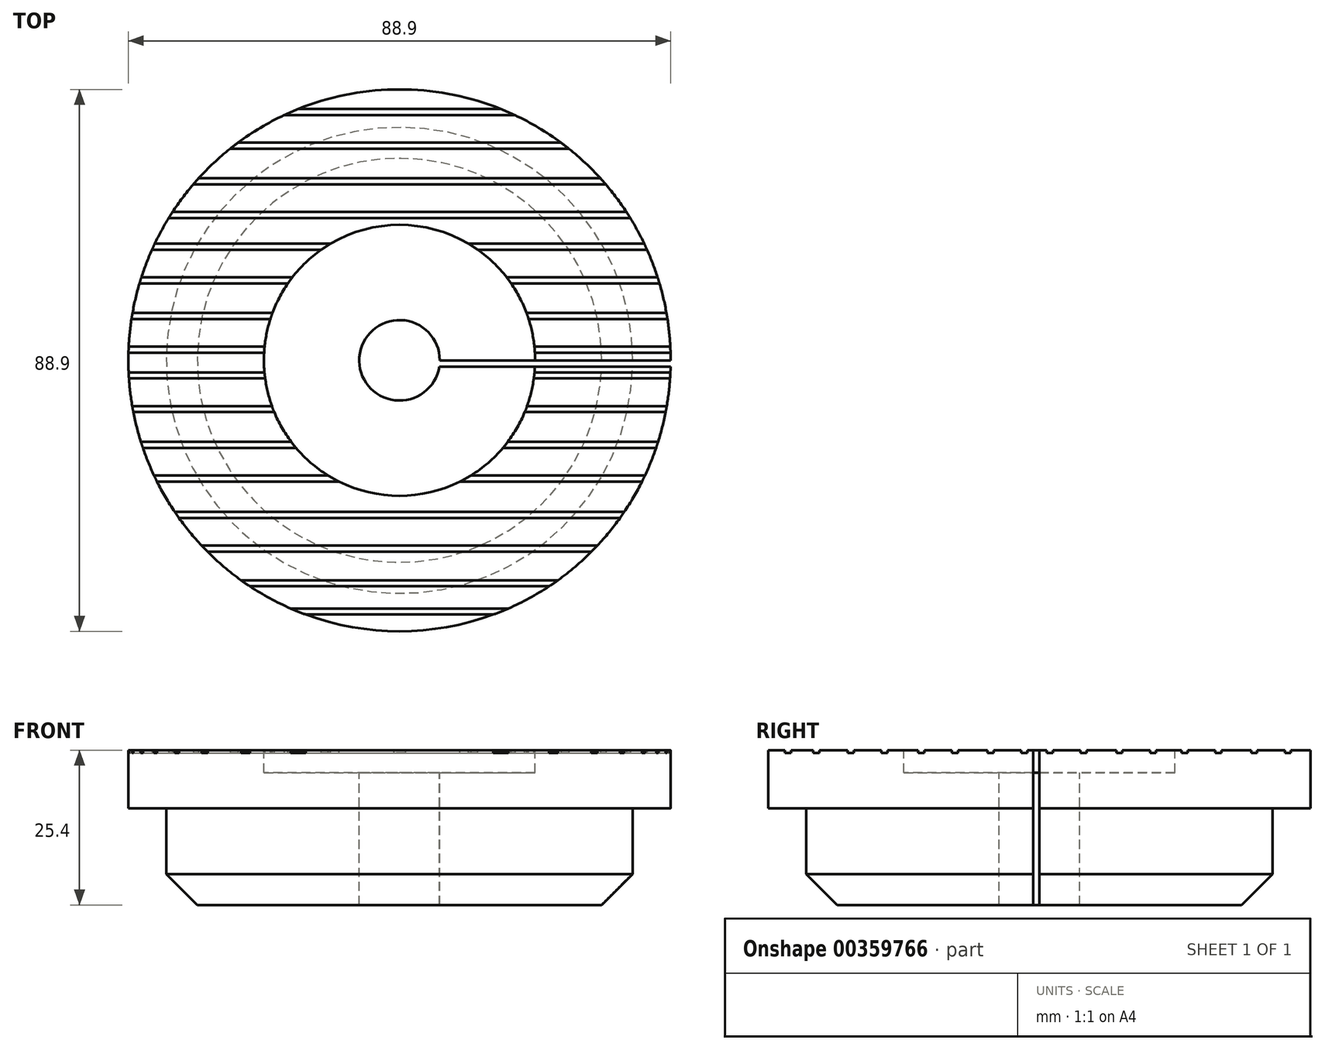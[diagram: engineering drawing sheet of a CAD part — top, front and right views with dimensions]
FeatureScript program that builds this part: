
annotation { "Feature Type Name" : "Feature", "Feature Type Description" : "" }
export const myFeature = defineFeature(function(context is Context, id is Id, definition is map)
    precondition{}
    {
        {
            var Q0;
            Q0=qCreatedBy(makeId("Front.planeOp"),FACE);
            var sketch = newSketch(context, id + "F0", { "sketchPlane" : qUnion([Q0])});
            skLineSegment(sketch, "E0", {"start": v(0, 0) * mm, "end": v(0, 38.13) * mm});
            skLineSegment(sketch, "E1", {"start": v(0, 38.13) * mm, "end": v(0, 38.13) * mm});
            skLineSegment(sketch, "E2", {"start": v(0, 25.4) * mm, "end": v(0, 38.13) * mm});
            skLineSegment(sketch, "E3", {"start": v(0, 25.4) * mm, "end": v(-44.45, 25.4) * mm});
            skLineSegment(sketch, "E4", {"start": v(-44.45, 25.4) * mm, "end": v(-44.45, 15.88) * mm});
            skLineSegment(sketch, "E5", {"start": v(-44.45, 15.88) * mm, "end": v(-38.23, 15.88) * mm});
            skLineSegment(sketch, "E6", {"start": v(-38.23, 15.88) * mm, "end": v(-38.23, 0) * mm});
            skLineSegment(sketch, "E7", {"start": v(-38.23, 0) * mm, "end": v(0, 0) * mm});
            skSolve(sketch);
        }
        {
            var Q0;
            Q0 = qSketchRegion(id + "F0", true);
            var Q1;
            Q1=sQuery(id+"F0.wireOp",EDGE,"E0");
            revolve(context, id + "F1", {"entities" : qUnion([Q0]), "axis" : qUnion([Q1]), "revolveType" : RevolveType.FULL});
        }
        {
            var Q0;
            Q0=makeQuery(id+"F1.opRevolve","SWEPT_FACE",FACE,{"disambiguationData":[OSD([sQuery(id+"F0.wireOp",EDGE,"E3")])]});
            var sketch = newSketch(context, id + "F2", { "sketchPlane" : qUnion([Q0])});
            skPoint(sketch, "E8", {"position": v(0, 0) * mm});
            skLineSegment(sketch, "E9.bottom", {"start": v(44.34, -3.17) * mm, "end": v(-44.34, -3.18) * mm});
            skLineSegment(sketch, "E9.top", {"start": v(44.34, 3.18) * mm, "end": v(-44.34, 3.17) * mm});
            skLineSegment(sketch, "E9.left", {"start": v(44.34, -3.17) * mm, "end": v(44.34, 3.18) * mm});
            skLineSegment(sketch, "E9.right", {"start": v(-44.34, -3.18) * mm, "end": v(-44.34, 3.17) * mm});
            skLineSegment(sketch, "E10.bottom", {"start": v(10.32, -27.2) * mm, "end": v(23.02, -27.2) * mm});
            skLineSegment(sketch, "E10.top", {"start": v(10.32, -46.26) * mm, "end": v(23.02, -46.26) * mm});
            skLineSegment(sketch, "E10.left", {"start": v(10.32, -27.2) * mm, "end": v(10.32, -46.26) * mm});
            skLineSegment(sketch, "E10.right", {"start": v(23.02, -27.2) * mm, "end": v(23.02, -46.26) * mm});
            skLineSegment(sketch, "E11.bottom", {"start": v(0, 0) * mm, "end": v(50.8, 0) * mm});
            skLineSegment(sketch, "E11.top", {"start": v(0, -1.02) * mm, "end": v(50.8, -1.02) * mm});
            skLineSegment(sketch, "E11.left", {"start": v(0, 0) * mm, "end": v(0, -1.02) * mm});
            skLineSegment(sketch, "E11.right", {"start": v(50.8, 0) * mm, "end": v(50.8, -1.02) * mm});
            skSolve(sketch);
        }
        {
            var Q0;
            Q0=sQuery(id+"F2.wireOp",VERTEX,"E8");
            var Q1;
            Q1=makeQuery(id+"F1.opRevolve","SWEPT_BODY",BODY,{"disambiguationData":[OSD([sQuery(id+"F0.wireOp",EDGE,"E0"),sQuery(id+"F0.wireOp",EDGE,"E3"),sQuery(id+"F0.wireOp",EDGE,"E4"),sQuery(id+"F0.wireOp",EDGE,"E5"),sQuery(id+"F0.wireOp",EDGE,"E6"),sQuery(id+"F0.wireOp",EDGE,"E7")])]});
            hole(context, id + "F3", {"style" : HoleStyle.C_BORE, "endStyle" : HoleEndStyle.THROUGH, "holeDiameter" : 13.2 * mm, "cBoreDiameter" : .875 * 50.8 * mm, "cBoreDepth" : 3.68 * mm, "isTappedThrough" : true, "tappedDepth" : 12.7 * mm, "tapClearance" : 3, "locations" : qUnion([Q0]), "scope" : qUnion([Q1])});
        }
        {
            var Q0;
            Q0=makeQuery(id+"F2.imprint","IMPRINT",FACE,{"disambiguationData":[TD([[makeQuery(id+"F2.imprint","IMPRINT",EDGE,{"derivedFrom":sQuery(id+"F2.wireOp",EDGE,"E11.bottom")}),-1.0]])]});
            extrude(context, id + "F4", {"entities" : qUnion([Q0]), "operationType" : NewBodyOperationType.REMOVE, "oppositeDirection" : true, "depth" : 38.1 * mm});
        }
        {
            var Q0;
            Q0=makeQuery(id+"F1.opRevolve","SWEPT_EDGE",EDGE,{"disambiguationData":[OSD([sQuery(id+"F0.wireOp",EDGE,"E6"),sQuery(id+"F0.wireOp",EDGE,"E7")])]});
            chamfer(context, id + "F5", {"entities" : qUnion([Q0]), "width" : 5.08 * mm, "tangentPropagation" : true});
        }
        {
            var Q0;
            Q0=makeQuery(id+"F1.opRevolve","SWEPT_FACE",FACE,{"disambiguationData":[OSD([sQuery(id+"F0.wireOp",EDGE,"E3")])]});
            var sketch = newSketch(context, id + "F6", { "sketchPlane" : qUnion([Q0])});
            skLineSegment(sketch, "E12.bottom", {"start": v(-50.8, -25.88) * mm, "end": v(50.8, -25.88) * mm});
            skLineSegment(sketch, "E12.top", {"start": v(-50.8, -24.88) * mm, "end": v(50.8, -24.88) * mm});
            skLineSegment(sketch, "E12.left", {"start": v(-50.8, -25.88) * mm, "end": v(-50.8, -24.88) * mm});
            skLineSegment(sketch, "E12.right", {"start": v(50.8, -25.88) * mm, "end": v(50.8, -24.88) * mm});
            skPoint(sketch, "E12.middle", {"position": v(0, -25.38) * mm});
            skLineSegment(sketch, "E13.bottom", {"start": v(-50.8, -31.4) * mm, "end": v(50.8, -31.4) * mm});
            skLineSegment(sketch, "E13.top", {"start": v(-50.8, -30.4) * mm, "end": v(50.8, -30.4) * mm});
            skLineSegment(sketch, "E13.left", {"start": v(-50.8, -31.4) * mm, "end": v(-50.8, -30.4) * mm});
            skLineSegment(sketch, "E13.right", {"start": v(50.8, -31.4) * mm, "end": v(50.8, -30.4) * mm});
            skPoint(sketch, "E13.middle", {"position": v(0, -30.9) * mm});
            skLineSegment(sketch, "E14.bottom", {"start": v(-48.25, -37.08) * mm, "end": v(53.35, -37.08) * mm});
            skLineSegment(sketch, "E14.top", {"start": v(-48.25, -36.08) * mm, "end": v(53.35, -36.08) * mm});
            skLineSegment(sketch, "E14.left", {"start": v(-48.25, -37.08) * mm, "end": v(-48.25, -36.08) * mm});
            skLineSegment(sketch, "E14.right", {"start": v(53.35, -37.08) * mm, "end": v(53.35, -36.08) * mm});
            skPoint(sketch, "E14.middle", {"position": v(2.55, -36.58) * mm});
            skLineSegment(sketch, "E15.bottom", {"start": v(-50.47, 44.44) * mm, "end": v(51.13, 44.44) * mm});
            skLineSegment(sketch, "E15.top", {"start": v(-50.47, 45.44) * mm, "end": v(51.13, 45.44) * mm});
            skLineSegment(sketch, "E15.left", {"start": v(-50.47, 44.44) * mm, "end": v(-50.47, 45.44) * mm});
            skLineSegment(sketch, "E15.right", {"start": v(51.13, 44.44) * mm, "end": v(51.13, 45.44) * mm});
            skPoint(sketch, "E15.middle", {"position": v(0.33, 44.94) * mm});
            skLineSegment(sketch, "E16.bottom", {"start": v(-50.5, 40.23) * mm, "end": v(51.1, 40.23) * mm});
            skLineSegment(sketch, "E16.top", {"start": v(-50.5, 41.23) * mm, "end": v(51.1, 41.23) * mm});
            skLineSegment(sketch, "E16.left", {"start": v(-50.5, 40.23) * mm, "end": v(-50.5, 41.23) * mm});
            skLineSegment(sketch, "E16.right", {"start": v(51.1, 40.23) * mm, "end": v(51.1, 41.23) * mm});
            skPoint(sketch, "E16.middle", {"position": v(0.3, 40.73) * mm});
            skLineSegment(sketch, "E17.bottom", {"start": v(-50.5, 34.7) * mm, "end": v(51.1, 34.7) * mm});
            skLineSegment(sketch, "E17.top", {"start": v(-50.5, 35.7) * mm, "end": v(51.1, 35.7) * mm});
            skLineSegment(sketch, "E17.left", {"start": v(-50.5, 34.7) * mm, "end": v(-50.5, 35.7) * mm});
            skLineSegment(sketch, "E17.right", {"start": v(51.1, 34.7) * mm, "end": v(51.1, 35.7) * mm});
            skPoint(sketch, "E17.middle", {"position": v(0.3, 35.2) * mm});
            skLineSegment(sketch, "E18.bottom", {"start": v(-50.16, 28.85) * mm, "end": v(51.44, 28.85) * mm});
            skLineSegment(sketch, "E18.top", {"start": v(-50.16, 29.85) * mm, "end": v(51.44, 29.85) * mm});
            skLineSegment(sketch, "E18.left", {"start": v(-50.16, 28.85) * mm, "end": v(-50.16, 29.85) * mm});
            skLineSegment(sketch, "E18.right", {"start": v(51.44, 28.85) * mm, "end": v(51.44, 29.85) * mm});
            skPoint(sketch, "E18.middle", {"position": v(0.64, 29.35) * mm});
            skLineSegment(sketch, "E19.bottom", {"start": v(-50.16, 23.32) * mm, "end": v(51.44, 23.32) * mm});
            skLineSegment(sketch, "E19.top", {"start": v(-50.16, 24.32) * mm, "end": v(51.44, 24.32) * mm});
            skLineSegment(sketch, "E19.left", {"start": v(-50.16, 23.32) * mm, "end": v(-50.16, 24.32) * mm});
            skLineSegment(sketch, "E19.right", {"start": v(51.44, 23.32) * mm, "end": v(51.44, 24.32) * mm});
            skPoint(sketch, "E19.middle", {"position": v(0.64, 23.82) * mm});
            skLineSegment(sketch, "E20.bottom", {"start": v(-50.22, 18.14) * mm, "end": v(51.38, 18.14) * mm});
            skLineSegment(sketch, "E20.top", {"start": v(-50.22, 19.14) * mm, "end": v(51.38, 19.14) * mm});
            skLineSegment(sketch, "E20.left", {"start": v(-50.22, 18.14) * mm, "end": v(-50.22, 19.14) * mm});
            skLineSegment(sketch, "E20.right", {"start": v(51.38, 18.14) * mm, "end": v(51.38, 19.14) * mm});
            skPoint(sketch, "E20.middle", {"position": v(0.58, 18.64) * mm});
            skLineSegment(sketch, "E21.bottom", {"start": v(-50.22, 12.61) * mm, "end": v(51.38, 12.61) * mm});
            skLineSegment(sketch, "E21.top", {"start": v(-50.22, 13.61) * mm, "end": v(51.38, 13.61) * mm});
            skLineSegment(sketch, "E21.left", {"start": v(-50.22, 12.61) * mm, "end": v(-50.22, 13.61) * mm});
            skLineSegment(sketch, "E21.right", {"start": v(51.38, 12.61) * mm, "end": v(51.38, 13.61) * mm});
            skPoint(sketch, "E21.middle", {"position": v(0.58, 13.11) * mm});
            skLineSegment(sketch, "E22.bottom", {"start": v(-49.89, 6.76) * mm, "end": v(51.71, 6.76) * mm});
            skLineSegment(sketch, "E22.top", {"start": v(-49.89, 7.76) * mm, "end": v(51.71, 7.76) * mm});
            skLineSegment(sketch, "E22.left", {"start": v(-49.89, 6.76) * mm, "end": v(-49.89, 7.76) * mm});
            skLineSegment(sketch, "E22.right", {"start": v(51.71, 6.76) * mm, "end": v(51.71, 7.76) * mm});
            skPoint(sketch, "E22.middle", {"position": v(0.91, 7.26) * mm});
            skLineSegment(sketch, "E23.bottom", {"start": v(-49.89, 1.23) * mm, "end": v(51.71, 1.23) * mm});
            skLineSegment(sketch, "E23.top", {"start": v(-49.89, 2.23) * mm, "end": v(51.71, 2.23) * mm});
            skLineSegment(sketch, "E23.left", {"start": v(-49.89, 1.23) * mm, "end": v(-49.89, 2.23) * mm});
            skLineSegment(sketch, "E23.right", {"start": v(51.71, 1.23) * mm, "end": v(51.71, 2.23) * mm});
            skPoint(sketch, "E23.middle", {"position": v(0.91, 1.73) * mm});
            skLineSegment(sketch, "E24.bottom", {"start": v(-49.91, -2.98) * mm, "end": v(51.69, -2.98) * mm});
            skLineSegment(sketch, "E24.top", {"start": v(-49.91, -1.98) * mm, "end": v(51.69, -1.98) * mm});
            skLineSegment(sketch, "E24.left", {"start": v(-49.91, -2.98) * mm, "end": v(-49.91, -1.98) * mm});
            skLineSegment(sketch, "E24.right", {"start": v(51.69, -2.98) * mm, "end": v(51.69, -1.98) * mm});
            skPoint(sketch, "E24.middle", {"position": v(0.89, -2.48) * mm});
            skLineSegment(sketch, "E25.bottom", {"start": v(-49.91, -8.5) * mm, "end": v(51.69, -8.5) * mm});
            skLineSegment(sketch, "E25.top", {"start": v(-49.91, -7.5) * mm, "end": v(51.69, -7.5) * mm});
            skLineSegment(sketch, "E25.left", {"start": v(-49.91, -8.5) * mm, "end": v(-49.91, -7.5) * mm});
            skLineSegment(sketch, "E25.right", {"start": v(51.69, -8.5) * mm, "end": v(51.69, -7.5) * mm});
            skPoint(sketch, "E25.middle", {"position": v(0.89, -8) * mm});
            skLineSegment(sketch, "E26.bottom", {"start": v(-49.58, -14.36) * mm, "end": v(52.02, -14.36) * mm});
            skLineSegment(sketch, "E26.top", {"start": v(-49.58, -13.36) * mm, "end": v(52.02, -13.36) * mm});
            skLineSegment(sketch, "E26.left", {"start": v(-49.58, -14.36) * mm, "end": v(-49.58, -13.36) * mm});
            skLineSegment(sketch, "E26.right", {"start": v(52.02, -14.36) * mm, "end": v(52.02, -13.36) * mm});
            skPoint(sketch, "E26.middle", {"position": v(1.22, -13.86) * mm});
            skLineSegment(sketch, "E27.bottom", {"start": v(-49.58, -19.89) * mm, "end": v(52.02, -19.89) * mm});
            skLineSegment(sketch, "E27.top", {"start": v(-49.58, -18.89) * mm, "end": v(52.02, -18.89) * mm});
            skLineSegment(sketch, "E27.left", {"start": v(-49.58, -19.89) * mm, "end": v(-49.58, -18.89) * mm});
            skLineSegment(sketch, "E27.right", {"start": v(52.02, -19.89) * mm, "end": v(52.02, -18.89) * mm});
            skPoint(sketch, "E27.middle", {"position": v(1.22, -19.39) * mm});
            skLineSegment(sketch, "E28.bottom", {"start": v(-49.73, -41.7) * mm, "end": v(51.87, -41.7) * mm});
            skLineSegment(sketch, "E28.top", {"start": v(-49.73, -40.7) * mm, "end": v(51.87, -40.7) * mm});
            skLineSegment(sketch, "E28.left", {"start": v(-49.73, -41.7) * mm, "end": v(-49.73, -40.7) * mm});
            skLineSegment(sketch, "E28.right", {"start": v(51.87, -41.7) * mm, "end": v(51.87, -40.7) * mm});
            skPoint(sketch, "E28.middle", {"position": v(1.07, -41.2) * mm});
            skSolve(sketch);
        }
        {
            var Q0;
            Q0 = qSketchRegion(id + "F6", true);
            extrude(context, id + "F7", {"entities" : qUnion([Q0]), "operationType" : NewBodyOperationType.REMOVE, "oppositeDirection" : true, "depth" : 0.5 * mm});
        }
    });
